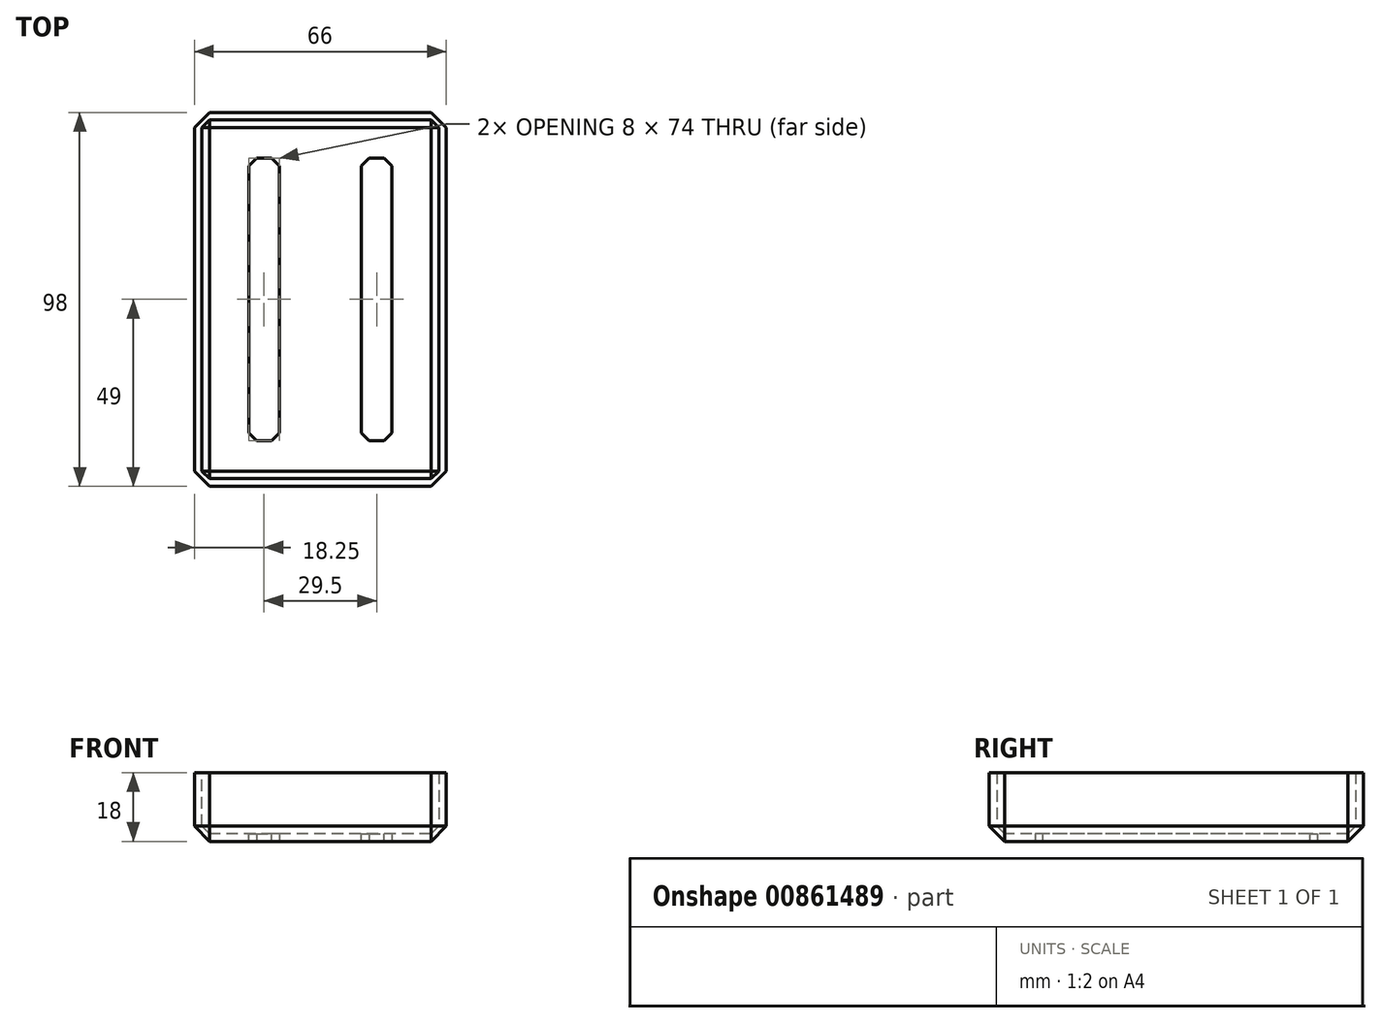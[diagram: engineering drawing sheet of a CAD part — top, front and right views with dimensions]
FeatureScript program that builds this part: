
annotation { "Feature Type Name" : "Feature", "Feature Type Description" : "" }
export const myFeature = defineFeature(function(context is Context, id is Id, definition is map)
    precondition{}
    {
        {
            var Q0;
            Q0=qCreatedBy(makeId("Top.planeOp"),FACE);
            var sketch = newSketch(context, id + "F0", { "sketchPlane" : qUnion([Q0])});
            skLineSegment(sketch, "E0.bottom", {"start": v(-33, -49) * mm, "end": v(33, -49) * mm});
            skLineSegment(sketch, "E0.top", {"start": v(-33, 49) * mm, "end": v(33, 49) * mm});
            skLineSegment(sketch, "E0.left", {"start": v(-33, -49) * mm, "end": v(-33, 49) * mm});
            skLineSegment(sketch, "E0.right", {"start": v(33, -49) * mm, "end": v(33, 49) * mm});
            skPoint(sketch, "E0.middle", {"position": v(0, 0) * mm});
            skLineSegment(sketch, "E1.bottom", {"start": v(-38, 44) * mm, "end": v(-33, 44) * mm});
            skLineSegment(sketch, "E1.top", {"start": v(-38, -44) * mm, "end": v(-33, -44) * mm});
            skLineSegment(sketch, "E1.left", {"start": v(-38, 44) * mm, "end": v(-38, -44) * mm});
            skPoint(sketch, "E1.middle", {"position": v(-33, 0) * mm});
            skLineSegment(sketch, "E2.bottom", {"start": v(-31, 47) * mm, "end": v(31, 47) * mm});
            skLineSegment(sketch, "E2.top", {"start": v(-31, -47) * mm, "end": v(31, -47) * mm});
            skLineSegment(sketch, "E2.left", {"start": v(-31, 47) * mm, "end": v(-31, -47) * mm});
            skLineSegment(sketch, "E2.right", {"start": v(31, 47) * mm, "end": v(31, -47) * mm});
            skLineSegment(sketch, "E3.bottom", {"start": v(-18.75, 37) * mm, "end": v(-10.75, 37) * mm});
            skLineSegment(sketch, "E3.top", {"start": v(-18.75, -37) * mm, "end": v(-10.75, -37) * mm});
            skLineSegment(sketch, "E3.left", {"start": v(-18.75, 37) * mm, "end": v(-18.75, -37) * mm});
            skLineSegment(sketch, "E3.right", {"start": v(-10.75, 37) * mm, "end": v(-10.75, -37) * mm});
            skPoint(sketch, "E3.middle", {"position": v(-14.75, 0) * mm});
            skLineSegment(sketch, "E4.bottom", {"start": v(10.75, 37) * mm, "end": v(18.75, 37) * mm});
            skLineSegment(sketch, "E4.top", {"start": v(10.75, -37) * mm, "end": v(18.75, -37) * mm});
            skLineSegment(sketch, "E4.left", {"start": v(10.75, 37) * mm, "end": v(10.75, -37) * mm});
            skLineSegment(sketch, "E4.right", {"start": v(18.75, 37) * mm, "end": v(18.75, -37) * mm});
            skPoint(sketch, "E4.middle", {"position": v(14.75, 0) * mm});
            skSolve(sketch);
        }
        {
            var Q0;
            Q0=makeQuery(id+"F0.imprint","IMPRINT",FACE,{"disambiguationData":[TD([[makeQuery(id+"F0.imprint","IMPRINT",EDGE,{"derivedFrom":sQuery(id+"F0.wireOp",EDGE,"E2.bottom")}),-1.0]])]});
            var Q1;
            {var subQ3=sQuery(id+"F0.wireOp",EDGE,"E0.bottom");Q1=makeQuery(id+"F0.imprint","IMPRINT",FACE,{"disambiguationData":[TD([[makeQuery(id+"F0.imprint","IMPRINT",EDGE,{"derivedFrom":subQ3}),1.0]])]});}
            extrude(context, id + "F1", {"entities" : qUnion([Q0, Q1]), "depth" : 2 * mm, "offsetDistance" : 25 * mm});
        }
        {
            var Q0;
            {var subQ3=sQuery(id+"F0.wireOp",EDGE,"E0.bottom");Q0=makeQuery(id+"F0.imprint","IMPRINT",FACE,{"disambiguationData":[TD([[makeQuery(id+"F0.imprint","IMPRINT",EDGE,{"derivedFrom":subQ3}),1.0]])]});}
            extrude(context, id + "F2", {"entities" : qUnion([Q0]), "operationType" : NewBodyOperationType.ADD, "depth" : 18 * mm, "offsetDistance" : 25 * mm});
        }
        {
            var Q0;
            Q0=makeQuery(id+"F2.opExtrude","SWEPT_EDGE",EDGE,{"disambiguationData":[OSD([sQuery(id+"F0.wireOp",EDGE,"E2.bottom"),sQuery(id+"F0.wireOp",EDGE,"E2.right")])]});
            var Q1;
            Q1=makeQuery(id+"F2.opExtrude","SWEPT_EDGE",EDGE,{"disambiguationData":[OSD([sQuery(id+"F0.wireOp",EDGE,"E2.bottom"),sQuery(id+"F0.wireOp",EDGE,"E2.left")])]});
            var Q2;
            Q2=makeQuery(id+"F2.opExtrude","SWEPT_EDGE",EDGE,{"disambiguationData":[OSD([sQuery(id+"F0.wireOp",EDGE,"E2.top"),sQuery(id+"F0.wireOp",EDGE,"E2.left")])]});
            var Q3;
            Q3=makeQuery(id+"F2.opExtrude","SWEPT_EDGE",EDGE,{"disambiguationData":[OSD([sQuery(id+"F0.wireOp",EDGE,"E2.top"),sQuery(id+"F0.wireOp",EDGE,"E2.right")])]});
            var Q4;
            Q4=makeQuery(id+"F1.opExtrude","SWEPT_EDGE",EDGE,{"disambiguationData":[OSD([sQuery(id+"F0.wireOp",EDGE,"E3.bottom"),sQuery(id+"F0.wireOp",EDGE,"E3.left")])]});
            var Q5;
            Q5=makeQuery(id+"F1.opExtrude","SWEPT_EDGE",EDGE,{"disambiguationData":[OSD([sQuery(id+"F0.wireOp",EDGE,"E4.bottom"),sQuery(id+"F0.wireOp",EDGE,"E4.left")])]});
            var Q6;
            Q6=makeQuery(id+"F1.opExtrude","SWEPT_EDGE",EDGE,{"disambiguationData":[OSD([sQuery(id+"F0.wireOp",EDGE,"E3.bottom"),sQuery(id+"F0.wireOp",EDGE,"E3.right")])]});
            var Q7;
            Q7=makeQuery(id+"F1.opExtrude","SWEPT_EDGE",EDGE,{"disambiguationData":[OSD([sQuery(id+"F0.wireOp",EDGE,"E4.bottom"),sQuery(id+"F0.wireOp",EDGE,"E4.right")])]});
            var Q8;
            Q8=makeQuery(id+"F1.opExtrude","SWEPT_EDGE",EDGE,{"disambiguationData":[OSD([sQuery(id+"F0.wireOp",EDGE,"E3.top"),sQuery(id+"F0.wireOp",EDGE,"E3.right")])]});
            var Q9;
            Q9=makeQuery(id+"F1.opExtrude","SWEPT_EDGE",EDGE,{"disambiguationData":[OSD([sQuery(id+"F0.wireOp",EDGE,"E4.top"),sQuery(id+"F0.wireOp",EDGE,"E4.right")])]});
            var Q10;
            Q10=makeQuery(id+"F1.opExtrude","SWEPT_EDGE",EDGE,{"disambiguationData":[OSD([sQuery(id+"F0.wireOp",EDGE,"E4.top"),sQuery(id+"F0.wireOp",EDGE,"E4.left")])]});
            var Q11;
            Q11=makeQuery(id+"F1.opExtrude","SWEPT_EDGE",EDGE,{"disambiguationData":[OSD([sQuery(id+"F0.wireOp",EDGE,"E3.top"),sQuery(id+"F0.wireOp",EDGE,"E3.left")])]});
            var Q12;
            Q12=makeQuery(id+"F2.boolean.opBoolean","INTERSECT",EDGE,{"derivedFrom":[makeQuery(id+"F1.opExtrude","CAP_FACE",FACE,{"disambiguationData":[OSD([sQuery(id+"F0.wireOp",EDGE,"E0.bottom"),sQuery(id+"F0.wireOp",EDGE,"E0.top"),sQuery(id+"F0.wireOp",EDGE,"E0.left"),sQuery(id+"F0.wireOp",EDGE,"E0.right"),sQuery(id+"F0.wireOp",EDGE,"E3.bottom"),sQuery(id+"F0.wireOp",EDGE,"E3.top"),sQuery(id+"F0.wireOp",EDGE,"E3.left"),sQuery(id+"F0.wireOp",EDGE,"E3.right"),sQuery(id+"F0.wireOp",EDGE,"E4.bottom"),sQuery(id+"F0.wireOp",EDGE,"E4.top"),sQuery(id+"F0.wireOp",EDGE,"E4.left"),sQuery(id+"F0.wireOp",EDGE,"E4.right")])],"isStart":false}),makeQuery(id+"F2.opExtrude","SWEPT_FACE",FACE,{"disambiguationData":[OSD([sQuery(id+"F0.wireOp",EDGE,"E2.left")])]})]});
            var Q13;
            Q13=makeQuery(id+"F2.boolean.opBoolean","INTERSECT",EDGE,{"derivedFrom":[makeQuery(id+"F1.opExtrude","CAP_FACE",FACE,{"disambiguationData":[OSD([sQuery(id+"F0.wireOp",EDGE,"E0.bottom"),sQuery(id+"F0.wireOp",EDGE,"E0.top"),sQuery(id+"F0.wireOp",EDGE,"E0.left"),sQuery(id+"F0.wireOp",EDGE,"E0.right"),sQuery(id+"F0.wireOp",EDGE,"E3.bottom"),sQuery(id+"F0.wireOp",EDGE,"E3.top"),sQuery(id+"F0.wireOp",EDGE,"E3.left"),sQuery(id+"F0.wireOp",EDGE,"E3.right"),sQuery(id+"F0.wireOp",EDGE,"E4.bottom"),sQuery(id+"F0.wireOp",EDGE,"E4.top"),sQuery(id+"F0.wireOp",EDGE,"E4.left"),sQuery(id+"F0.wireOp",EDGE,"E4.right")])],"isStart":false}),makeQuery(id+"F2.opExtrude","SWEPT_FACE",FACE,{"disambiguationData":[OSD([sQuery(id+"F0.wireOp",EDGE,"E2.bottom")])]})]});
            var Q14;
            Q14=makeQuery(id+"F2.boolean.opBoolean","INTERSECT",EDGE,{"derivedFrom":[makeQuery(id+"F1.opExtrude","CAP_FACE",FACE,{"disambiguationData":[OSD([sQuery(id+"F0.wireOp",EDGE,"E0.bottom"),sQuery(id+"F0.wireOp",EDGE,"E0.top"),sQuery(id+"F0.wireOp",EDGE,"E0.left"),sQuery(id+"F0.wireOp",EDGE,"E0.right"),sQuery(id+"F0.wireOp",EDGE,"E3.bottom"),sQuery(id+"F0.wireOp",EDGE,"E3.top"),sQuery(id+"F0.wireOp",EDGE,"E3.left"),sQuery(id+"F0.wireOp",EDGE,"E3.right"),sQuery(id+"F0.wireOp",EDGE,"E4.bottom"),sQuery(id+"F0.wireOp",EDGE,"E4.top"),sQuery(id+"F0.wireOp",EDGE,"E4.left"),sQuery(id+"F0.wireOp",EDGE,"E4.right")])],"isStart":false}),makeQuery(id+"F2.opExtrude","SWEPT_FACE",FACE,{"disambiguationData":[OSD([sQuery(id+"F0.wireOp",EDGE,"E2.right")])]})]});
            var Q15;
            Q15=makeQuery(id+"F2.boolean.opBoolean","INTERSECT",EDGE,{"derivedFrom":[makeQuery(id+"F1.opExtrude","CAP_FACE",FACE,{"disambiguationData":[OSD([sQuery(id+"F0.wireOp",EDGE,"E0.bottom"),sQuery(id+"F0.wireOp",EDGE,"E0.top"),sQuery(id+"F0.wireOp",EDGE,"E0.left"),sQuery(id+"F0.wireOp",EDGE,"E0.right"),sQuery(id+"F0.wireOp",EDGE,"E3.bottom"),sQuery(id+"F0.wireOp",EDGE,"E3.top"),sQuery(id+"F0.wireOp",EDGE,"E3.left"),sQuery(id+"F0.wireOp",EDGE,"E3.right"),sQuery(id+"F0.wireOp",EDGE,"E4.bottom"),sQuery(id+"F0.wireOp",EDGE,"E4.top"),sQuery(id+"F0.wireOp",EDGE,"E4.left"),sQuery(id+"F0.wireOp",EDGE,"E4.right")])],"isStart":false}),makeQuery(id+"F2.opExtrude","SWEPT_FACE",FACE,{"disambiguationData":[OSD([sQuery(id+"F0.wireOp",EDGE,"E2.top")])]})]});
            chamfer(context, id + "F3", {"entities" : qUnion([Q0, Q1, Q2, Q3, Q4, Q5, Q6, Q7, Q8, Q9, Q10, Q11, Q12, Q13, Q14, Q15]), "width" : 2 * mm, "tangentPropagation" : true});
        }
        {
            var Q0;
            {var subQ0=sQuery(id+"F0.wireOp",EDGE,"E0.left");var subQ1=sQuery(id+"F0.wireOp",EDGE,"E0.top");Q0=makeQuery(id+"F2.boolean.opBoolean","MERGE",EDGE,{"derivedFrom":[makeQuery(id+"F1.opExtrude","SWEPT_EDGE",EDGE,{"disambiguationData":[OSD([subQ1,subQ0])]}),makeQuery(id+"F2.opExtrude","SWEPT_EDGE",EDGE,{"disambiguationData":[OSD([subQ1,subQ0])]})]});}
            var Q1;
            {var subQ0=sQuery(id+"F0.wireOp",EDGE,"E0.right");var subQ1=sQuery(id+"F0.wireOp",EDGE,"E0.top");Q1=makeQuery(id+"F2.boolean.opBoolean","MERGE",EDGE,{"derivedFrom":[makeQuery(id+"F1.opExtrude","SWEPT_EDGE",EDGE,{"disambiguationData":[OSD([subQ1,subQ0])]}),makeQuery(id+"F2.opExtrude","SWEPT_EDGE",EDGE,{"disambiguationData":[OSD([subQ1,subQ0])]})]});}
            var Q2;
            {var subQ0=sQuery(id+"F0.wireOp",EDGE,"E0.right");var subQ1=sQuery(id+"F0.wireOp",EDGE,"E0.bottom");Q2=makeQuery(id+"F2.boolean.opBoolean","MERGE",EDGE,{"derivedFrom":[makeQuery(id+"F1.opExtrude","SWEPT_EDGE",EDGE,{"disambiguationData":[OSD([subQ1,subQ0])]}),makeQuery(id+"F2.opExtrude","SWEPT_EDGE",EDGE,{"disambiguationData":[OSD([subQ1,subQ0])]})]});}
            var Q3;
            {var subQ0=sQuery(id+"F0.wireOp",EDGE,"E0.left");var subQ1=sQuery(id+"F0.wireOp",EDGE,"E0.bottom");Q3=makeQuery(id+"F2.boolean.opBoolean","MERGE",EDGE,{"derivedFrom":[makeQuery(id+"F1.opExtrude","SWEPT_EDGE",EDGE,{"disambiguationData":[OSD([subQ1,subQ0])]}),makeQuery(id+"F2.opExtrude","SWEPT_EDGE",EDGE,{"disambiguationData":[OSD([subQ1,subQ0])]})]});}
            var Q4;
            Q4=makeQuery(id+"F1.opExtrude","CAP_EDGE",EDGE,{"disambiguationData":[OSD([sQuery(id+"F0.wireOp",EDGE,"E0.left")])],"isStart":true});
            var Q5;
            Q5=makeQuery(id+"F1.opExtrude","CAP_EDGE",EDGE,{"disambiguationData":[OSD([sQuery(id+"F0.wireOp",EDGE,"E0.right")])],"isStart":true});
            var Q6;
            Q6=makeQuery(id+"F1.opExtrude","CAP_EDGE",EDGE,{"disambiguationData":[OSD([sQuery(id+"F0.wireOp",EDGE,"E0.bottom")])],"isStart":true});
            var Q7;
            Q7=makeQuery(id+"F1.opExtrude","CAP_EDGE",EDGE,{"disambiguationData":[OSD([sQuery(id+"F0.wireOp",EDGE,"E0.top")])],"isStart":true});
            chamfer(context, id + "F4", {"entities" : qUnion([Q0, Q1, Q2, Q3, Q4, Q5, Q6, Q7]), "width" : 4 * mm, "tangentPropagation" : true});
        }
    });
